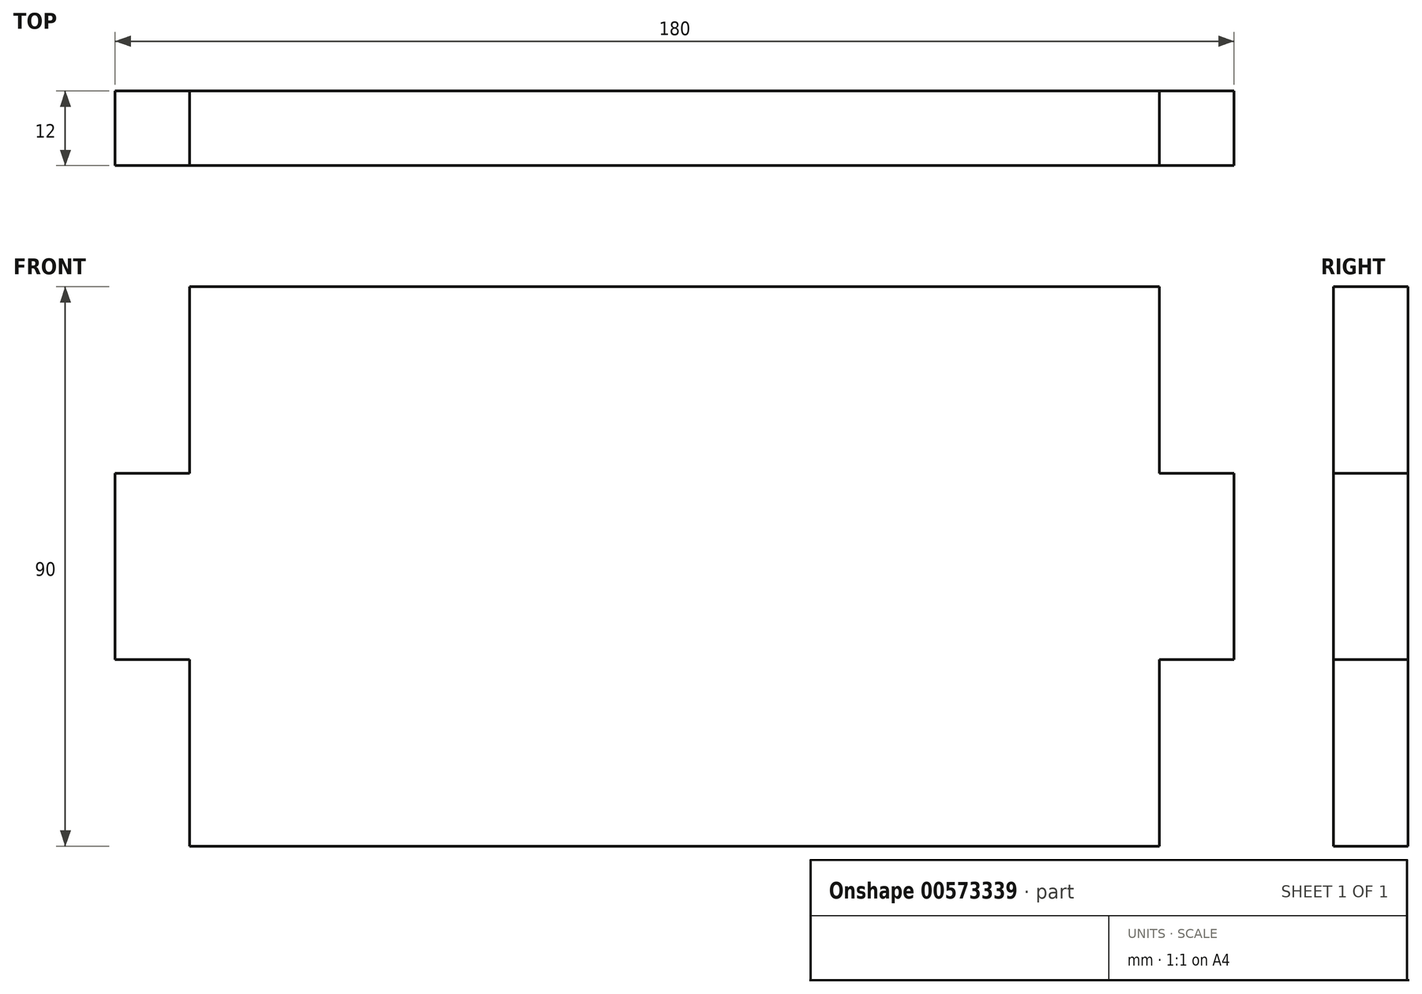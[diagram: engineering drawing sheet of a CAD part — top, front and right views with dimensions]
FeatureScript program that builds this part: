
annotation { "Feature Type Name" : "Feature", "Feature Type Description" : "" }
export const myFeature = defineFeature(function(context is Context, id is Id, definition is map)
    precondition{}
    {
        {
            var Q0;
            Q0=qCreatedBy(makeId("Front.planeOp"),FACE);
            var sketch = newSketch(context, id + "F0", { "sketchPlane" : qUnion([Q0])});
            skLineSegment(sketch, "E0", {"start": v(0, -12.43) * mm, "end": v(0, 17.57) * mm});
            skLineSegment(sketch, "E1", {"start": v(0, 17.57) * mm, "end": v(-12, 17.57) * mm});
            skLineSegment(sketch, "E2", {"start": v(-12, 17.57) * mm, "end": v(-12, 47.57) * mm});
            skLineSegment(sketch, "E3", {"start": v(-12, 47.57) * mm, "end": v(0, 47.57) * mm});
            skLineSegment(sketch, "E4", {"start": v(0, 47.57) * mm, "end": v(0, 77.57) * mm});
            skLineSegment(sketch, "E5", {"start": v(0, 77.57) * mm, "end": v(78, 77.57) * mm});
            skLineSegment(sketch, "E6", {"start": v(78, 77.57) * mm, "end": v(78, -12.43) * mm, "construction": true});
            skLineSegment(sketch, "E7", {"start": v(78, -12.43) * mm, "end": v(0, -12.43) * mm});
            skLineSegment(sketch, "E8.MirrorCS", {"start": v(156, 17.57) * mm, "end": v(168, 17.57) * mm});
            skLineSegment(sketch, "E9.MirrorCS", {"start": v(168, 17.57) * mm, "end": v(168, 47.57) * mm});
            skLineSegment(sketch, "E10.MirrorCS", {"start": v(168, 47.57) * mm, "end": v(156, 47.57) * mm});
            skLineSegment(sketch, "E11.MirrorCS", {"start": v(156, 47.57) * mm, "end": v(156, 77.57) * mm});
            skLineSegment(sketch, "E12.MirrorCS", {"start": v(156, -12.43) * mm, "end": v(156, 17.57) * mm});
            skLineSegment(sketch, "E13.MirrorCS", {"start": v(156, 77.57) * mm, "end": v(78, 77.57) * mm});
            skLineSegment(sketch, "E14.MirrorCS", {"start": v(78, -12.43) * mm, "end": v(156, -12.43) * mm});
            skSolve(sketch);
        }
        {
            var Q0;
            Q0 = qSketchRegion(id + "F0", true);
            extrude(context, id + "F1", {"entities" : qUnion([Q0]), "endBound" : BoundingType.SYMMETRIC, "depth" : 12 * mm, "offsetDistance" : 25 * mm});
        }
    });
